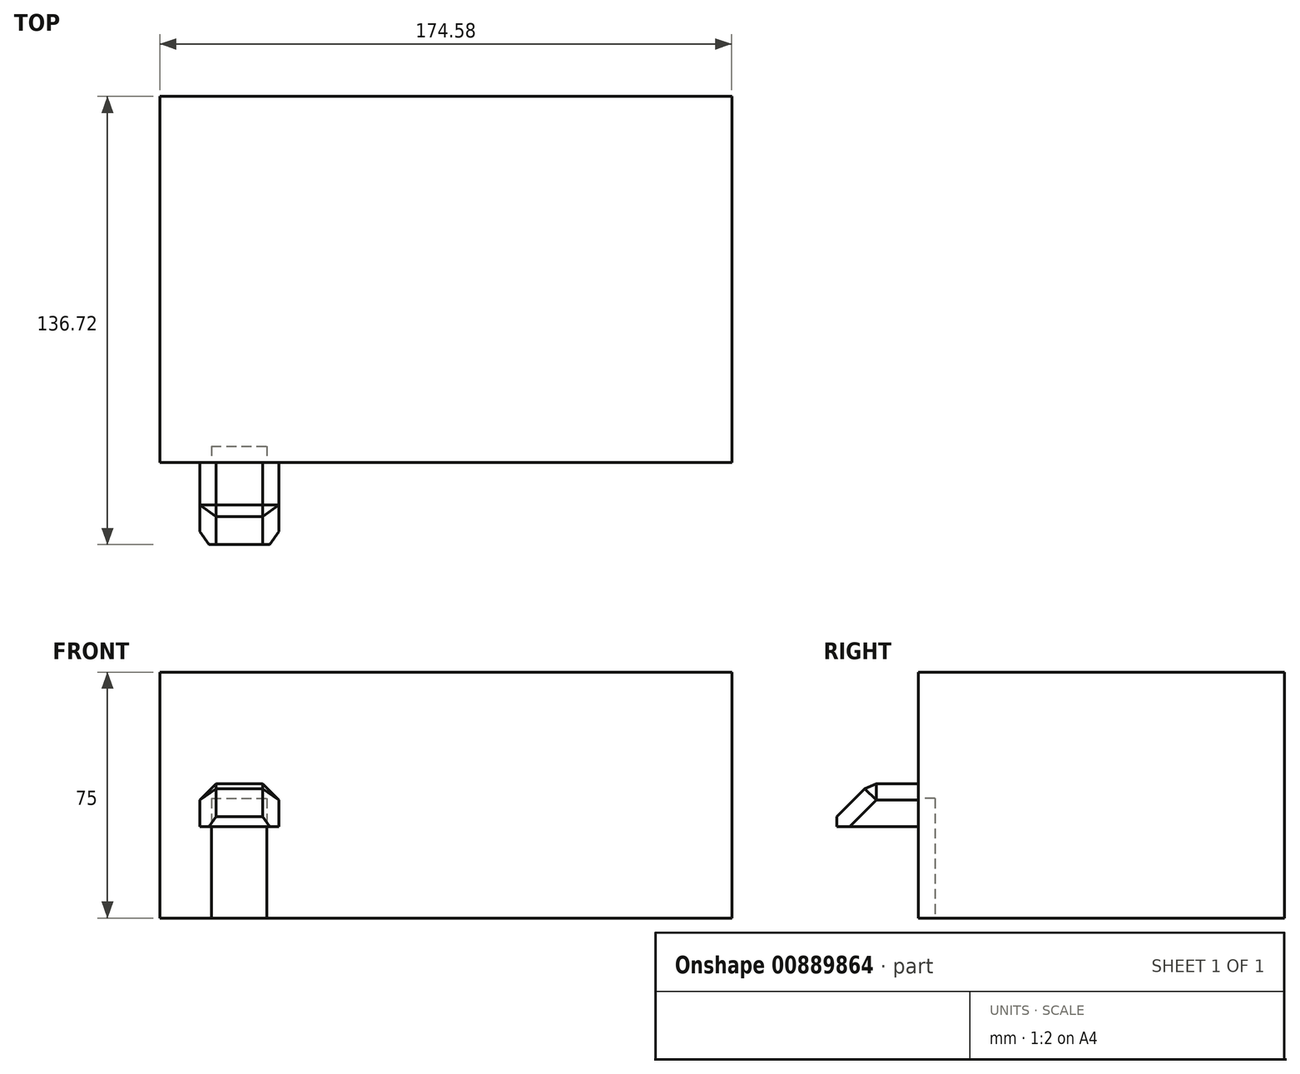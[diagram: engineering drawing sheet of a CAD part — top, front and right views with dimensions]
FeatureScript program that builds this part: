
annotation { "Feature Type Name" : "Feature", "Feature Type Description" : "" }
export const myFeature = defineFeature(function(context is Context, id is Id, definition is map)
    precondition{}
    {
        {
            var Q0;
            Q0=qCreatedBy(makeId("Top.planeOp"),FACE);
            var sketch = newSketch(context, id + "F0", { "sketchPlane" : qUnion([Q0])});
            skLineSegment(sketch, "E0.bottom", {"start": v(-74.94, 55.77) * mm, "end": v(99.64, 55.77) * mm});
            skLineSegment(sketch, "E0.top", {"start": v(-74.94, -55.95) * mm, "end": v(99.64, -55.95) * mm});
            skLineSegment(sketch, "E0.left", {"start": v(-74.94, 55.77) * mm, "end": v(-74.94, -55.95) * mm});
            skLineSegment(sketch, "E0.right", {"start": v(99.64, 55.77) * mm, "end": v(99.64, -55.95) * mm});
            skSolve(sketch);
        }
        {
            var Q0;
            Q0 = qSketchRegion(id + "F0", true);
            extrude(context, id + "F1", {"entities" : qUnion([Q0]), "depth" : 100 * mm, "offsetDistance" : 25 * mm});
        }
        {
            var Q0;
            Q0=makeQuery(id+"F1.opExtrude","SWEPT_FACE",FACE,{"disambiguationData":[OSD([sQuery(id+"F0.wireOp",EDGE,"E0.top")])]});
            var sketch = newSketch(context, id + "F2", { "sketchPlane" : qUnion([Q0])});
            skSolve(sketch);
        }
        {
            var Q0;
            {var subQ0=sQuery(id+"F0.wireOp",EDGE,"E0.top");Q0=makeQuery(id+"F2.imprint","IMPRINT",FACE,{"disambiguationData":[TD([[makeQuery(id+"F2.imprint","IMPRINT",EDGE,{"derivedFrom":makeQuery(id+"F1.opExtrude","CAP_EDGE",EDGE,{"disambiguationData":[OSD([subQ0])],"isStart":true})}),1.0]])]});}
            var sketch = newSketch(context, id + "F3", { "sketchPlane" : qUnion([Q0])});
            skLineSegment(sketch, "E1.bottom", {"start": v(-59.21, 36.48) * mm, "end": v(-42.23, 36.48) * mm});
            skLineSegment(sketch, "E1.top", {"start": v(-59.21, 0) * mm, "end": v(-42.23, 0) * mm});
            skLineSegment(sketch, "E1.left", {"start": v(-59.21, 36.48) * mm, "end": v(-59.21, 0) * mm});
            skLineSegment(sketch, "E1.right", {"start": v(-42.23, 36.48) * mm, "end": v(-42.23, 0) * mm});
            skSolve(sketch);
        }
        {
            var Q0;
            Q0 = qSketchRegion(id + "F3", true);
            extrude(context, id + "F4", {"entities" : qUnion([Q0]), "operationType" : NewBodyOperationType.REMOVE, "oppositeDirection" : true, "depth" : 5 * mm, "offsetDistance" : 25 * mm});
        }
        {
            var Q0;
            Q0=makeQuery(id+"F1.opExtrude","CAP_FACE",FACE,{"disambiguationData":[OSD([sQuery(id+"F0.wireOp",EDGE,"E0.bottom"),sQuery(id+"F0.wireOp",EDGE,"E0.top"),sQuery(id+"F0.wireOp",EDGE,"E0.left"),sQuery(id+"F0.wireOp",EDGE,"E0.right")])],"isStart":false});
            var sketch = newSketch(context, id + "F5", { "sketchPlane" : qUnion([Q0])});
            skLineSegment(sketch, "E2.bottom", {"start": v(-74.94, 55.77) * mm, "end": v(99.64, 55.77) * mm});
            skLineSegment(sketch, "E2.top", {"start": v(-74.94, -55.95) * mm, "end": v(99.64, -55.95) * mm});
            skLineSegment(sketch, "E2.left", {"start": v(-74.94, 55.77) * mm, "end": v(-74.94, -55.95) * mm});
            skLineSegment(sketch, "E2.right", {"start": v(99.64, 55.77) * mm, "end": v(99.64, -55.95) * mm});
            skSolve(sketch);
        }
        {
            var Q0;
            Q0 = qSketchRegion(id + "F5", true);
            extrude(context, id + "F6", {"entities" : qUnion([Q0]), "operationType" : NewBodyOperationType.REMOVE, "oppositeDirection" : true, "depth" : 25 * mm, "offsetDistance" : 25 * mm});
        }
        {
            var Q0;
            {var subQ0=sQuery(id+"F0.wireOp",EDGE,"E0.top");Q0=makeQuery(id+"F2.imprint","IMPRINT",FACE,{"disambiguationData":[TD([[makeQuery(id+"F2.imprint","IMPRINT",EDGE,{"derivedFrom":makeQuery(id+"F1.opExtrude","CAP_EDGE",EDGE,{"disambiguationData":[OSD([subQ0])],"isStart":true})}),1.0]])]});}
            var sketch = newSketch(context, id + "F7", { "sketchPlane" : qUnion([Q0])});
            skLineSegment(sketch, "E3.bottom", {"start": v(-38.6, 27.85) * mm, "end": v(-62.72, 27.85) * mm});
            skLineSegment(sketch, "E3.top", {"start": v(-38.6, 40.97) * mm, "end": v(-62.72, 40.97) * mm});
            skLineSegment(sketch, "E3.left", {"start": v(-38.6, 27.85) * mm, "end": v(-38.6, 40.97) * mm});
            skLineSegment(sketch, "E3.right", {"start": v(-62.72, 27.85) * mm, "end": v(-62.72, 40.97) * mm});
            skSolve(sketch);
        }
        {
            var Q0;
            Q0 = qSketchRegion(id + "F7", true);
            extrude(context, id + "F8", {"entities" : qUnion([Q0]), "operationType" : NewBodyOperationType.ADD, "depth" : 25 * mm, "offsetDistance" : 25 * mm});
        }
        {
            var Q0;
            Q0=makeQuery(id+"F8.opExtrude","CAP_EDGE",EDGE,{"disambiguationData":[OSD([sQuery(id+"F7.wireOp",EDGE,"E3.top")])],"isStart":false});
            chamfer(context, id + "F9", {"entities" : qUnion([Q0]), "width" : 10 * mm, "tangentPropagation" : true});
        }
        {
            var Q0;
            Q0=makeQuery(id+"F8.opExtrude","SWEPT_EDGE",EDGE,{"disambiguationData":[OSD([sQuery(id+"F7.wireOp",EDGE,"E3.top"),sQuery(id+"F7.wireOp",EDGE,"E3.right")])]});
            var Q1;
            Q1=makeQuery(id+"F9.opChamfer","BLEND_EDGE",EDGE,{"blendedFrom":[makeQuery(id+"F8.opExtrude","CAP_EDGE",EDGE,{"disambiguationData":[OSD([sQuery(id+"F7.wireOp",EDGE,"E3.top")])],"isStart":false}),makeQuery(id+"F8.opExtrude","SWEPT_FACE",FACE,{"disambiguationData":[OSD([sQuery(id+"F7.wireOp",EDGE,"E3.left")])]})],"blendedInto":[makeQuery(id+"F8.opExtrude","SWEPT_FACE",FACE,{"disambiguationData":[OSD([sQuery(id+"F7.wireOp",EDGE,"E3.left")])]})]});
            var Q2;
            Q2=makeQuery(id+"F8.opExtrude","SWEPT_EDGE",EDGE,{"disambiguationData":[OSD([sQuery(id+"F7.wireOp",EDGE,"E3.top"),sQuery(id+"F7.wireOp",EDGE,"E3.left")])]});
            var Q3;
            Q3=makeQuery(id+"F9.opChamfer","BLEND_EDGE",EDGE,{"blendedFrom":[makeQuery(id+"F8.opExtrude","CAP_EDGE",EDGE,{"disambiguationData":[OSD([sQuery(id+"F7.wireOp",EDGE,"E3.top")])],"isStart":false}),makeQuery(id+"F8.opExtrude","SWEPT_FACE",FACE,{"disambiguationData":[OSD([sQuery(id+"F7.wireOp",EDGE,"E3.right")])]})],"blendedInto":[makeQuery(id+"F8.opExtrude","SWEPT_FACE",FACE,{"disambiguationData":[OSD([sQuery(id+"F7.wireOp",EDGE,"E3.right")])]})]});
            var Q4;
            {var subQ0=sQuery(id+"F7.wireOp",EDGE,"E3.top");Q4=makeQuery(id+"F9.opChamfer","BLEND_EDGE",EDGE,{"blendedFrom":[makeQuery(id+"F8.opExtrude","CAP_EDGE",EDGE,{"disambiguationData":[OSD([subQ0])],"isStart":false}),makeQuery(id+"F8.opExtrude","SWEPT_FACE",FACE,{"disambiguationData":[OSD([subQ0])]})],"blendedInto":[makeQuery(id+"F8.opExtrude","SWEPT_FACE",FACE,{"disambiguationData":[OSD([subQ0])]})]});}
            chamfer(context, id + "F10", {"entities" : qUnion([Q0, Q1, Q2, Q3, Q4]), "width" : 5 * mm, "tangentPropagation" : true});
        }
    });
